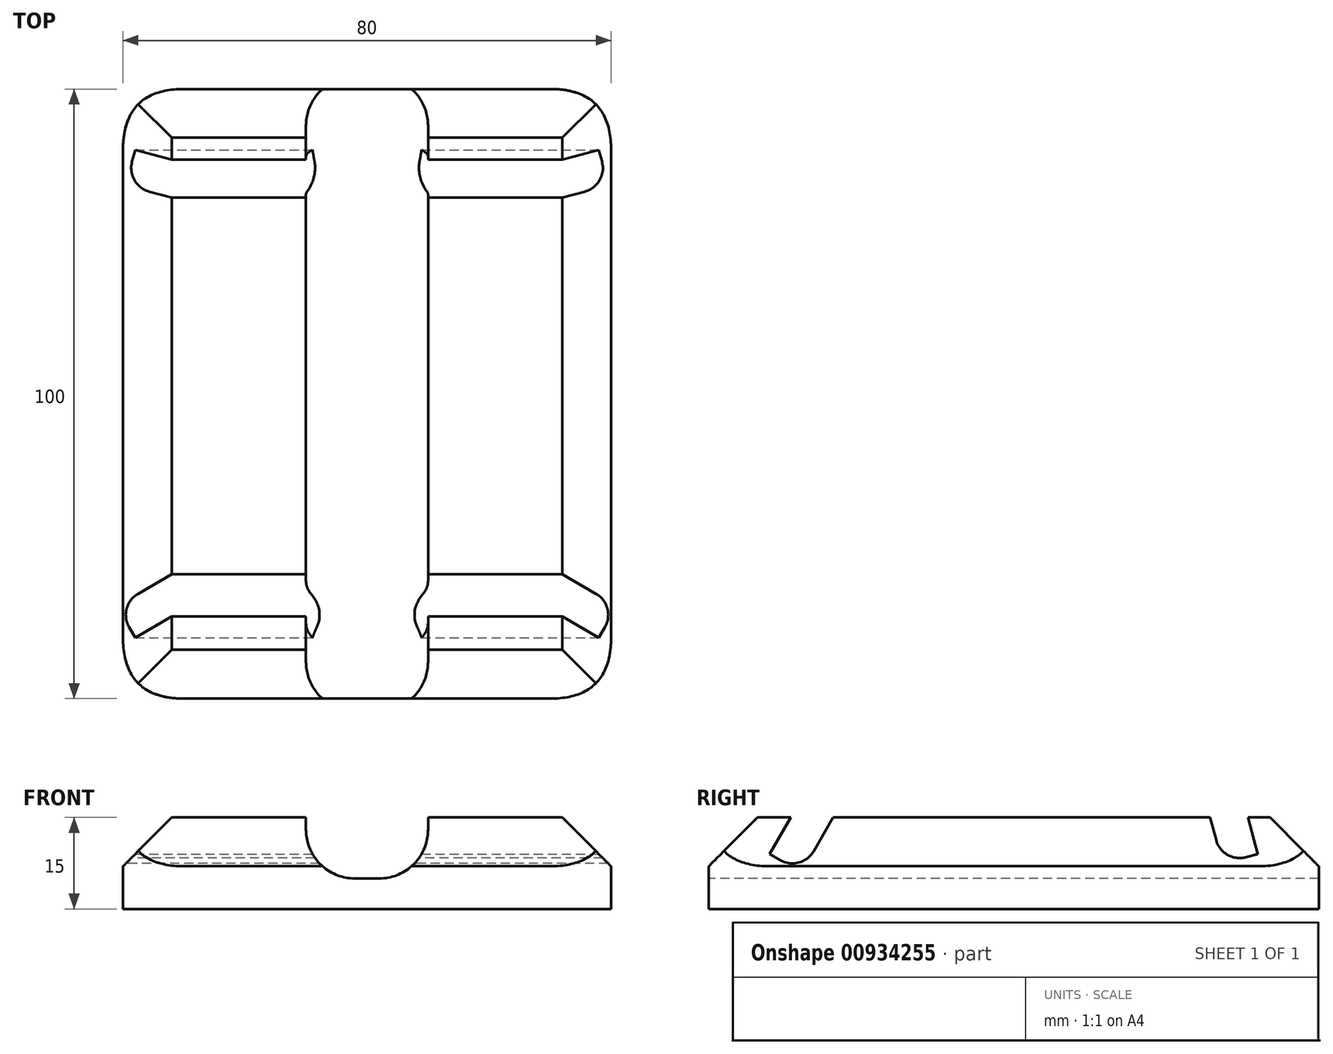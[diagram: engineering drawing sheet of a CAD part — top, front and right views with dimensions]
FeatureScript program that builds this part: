
annotation { "Feature Type Name" : "Feature", "Feature Type Description" : "" }
export const myFeature = defineFeature(function(context is Context, id is Id, definition is map)
    precondition{}
    {
        {
            var Q0;
            Q0=qCreatedBy(makeId("Right.planeOp"),FACE);
            var sketch = newSketch(context, id + "F0", { "sketchPlane" : qUnion([Q0])});
            skLineSegment(sketch, "E0.bottom", {"start": v(100, 15) * mm, "end": v(0, 15) * mm});
            skLineSegment(sketch, "E0.top", {"start": v(100, 0) * mm, "end": v(0, 0) * mm});
            skLineSegment(sketch, "E0.left", {"start": v(100, 15) * mm, "end": v(100, 0) * mm});
            skLineSegment(sketch, "E0.right", {"start": v(0, 15) * mm, "end": v(0, 0) * mm});
            skSolve(sketch);
        }
        {
            var Q0;
            Q0=makeQuery(id+"F0.imprint","IMPRINT",FACE,{"disambiguationData":[TD([[makeQuery(id+"F0.imprint","IMPRINT",EDGE,{"derivedFrom":sQuery(id+"F0.wireOp",EDGE,"E0.bottom")}),1.0]])]});
            var Q1;
            Q1=sQuery(id+"F0.wireOp",EDGE,"E0.bottom");
            var Q2;
            Q2 = qBodyType(qCreatedBy(id + "F0" ,EDGE), BodyType.WIRE);
            extrude(context, id + "F1", {"entities" : qUnion([Q0]), "surfaceEntities" : qUnion([Q1, Q2]), "endBound" : BoundingType.SYMMETRIC, "depth" : 80 * mm, "offsetDistance" : 25 * mm});
        }
        {
            var Q0;
            Q0=qCreatedBy(makeId("Right.planeOp"),FACE);
            var sketch = newSketch(context, id + "F2", { "sketchPlane" : qUnion([Q0])});
            skLineSegment(sketch, "E1", {"start": v(71.28, 9) * mm, "end": v(-12.51, 9) * mm, "construction": true});
            skLineSegment(sketch, "E2", {"start": v(10, 9) * mm, "end": v(97.5, 160.55) * mm, "construction": true});
            skLineSegment(sketch, "E3", {"start": v(90, 9) * mm, "end": v(44.7, 178.04) * mm, "construction": true});
            skLineSegment(sketch, "E4", {"start": v(44.7, 178.04) * mm, "end": v(25.3, 250.48) * mm, "construction": true});
            skLineSegment(sketch, "E5", {"start": v(135, 225.5) * mm, "end": v(97.5, 160.55) * mm, "construction": true});
            skSolve(sketch);
        }
        {
            var Q0;
            Q0=qCreatedBy(makeId("Right.planeOp"),FACE);
            var sketch = newSketch(context, id + "F3", { "sketchPlane" : qUnion([Q0])});
            skLineSegment(sketch, "E6", {"start": v(10, 9) * mm, "end": v(27.02, 38.48) * mm});
            skLineSegment(sketch, "E7", {"start": v(27.02, 38.48) * mm, "end": v(32.22, 35.48) * mm});
            skLineSegment(sketch, "E8", {"start": v(32.22, 35.48) * mm, "end": v(15.2, 6) * mm});
            skLineSegment(sketch, "E9", {"start": v(15.2, 6) * mm, "end": v(10, 9) * mm});
            skLineSegment(sketch, "E10", {"start": v(90, 9) * mm, "end": v(81.3, 41.48) * mm});
            skLineSegment(sketch, "E11", {"start": v(81.3, 41.48) * mm, "end": v(75.5, 39.93) * mm});
            skLineSegment(sketch, "E12", {"start": v(75.5, 39.93) * mm, "end": v(84.2, 7.45) * mm});
            skLineSegment(sketch, "E13", {"start": v(84.2, 7.45) * mm, "end": v(90, 9) * mm});
            skSolve(sketch);
        }
        {
            var Q0;
            Q0=makeQuery(id+"F1.opExtrude","CAP_EDGE",EDGE,{"disambiguationData":[OSD([sQuery(id+"F0.wireOp",EDGE,"E0.bottom")])],"isStart":false});
            var Q1;
            Q1=makeQuery(id+"F1.opExtrude","SWEPT_EDGE",EDGE,{"disambiguationData":[OSD([sQuery(id+"F0.wireOp",EDGE,"E0.bottom"),sQuery(id+"F0.wireOp",EDGE,"E0.right")])]});
            var Q2;
            Q2=makeQuery(id+"F1.opExtrude","CAP_EDGE",EDGE,{"disambiguationData":[OSD([sQuery(id+"F0.wireOp",EDGE,"E0.bottom")])],"isStart":true});
            var Q3;
            Q3=makeQuery(id+"F1.opExtrude","SWEPT_EDGE",EDGE,{"disambiguationData":[OSD([sQuery(id+"F0.wireOp",EDGE,"E0.bottom"),sQuery(id+"F0.wireOp",EDGE,"E0.left")])]});
            chamfer(context, id + "F4", {"entities" : qUnion([Q0, Q1, Q2, Q3]), "width" : 8 * mm, "tangentPropagation" : true});
        }
        {
            var Q0;
            Q0 = qSketchRegion(id + "F3", true);
            extrude(context, id + "F5", {"entities" : qUnion([Q0]), "operationType" : NewBodyOperationType.REMOVE, "endBound" : BoundingType.THROUGH_ALL, "oppositeDirection" : true, "depth" : 25 * mm, "offsetDistance" : 25 * mm, "hasSecondDirection" : true, "secondDirectionBound" : SecondDirectionBoundingType.THROUGH_ALL, "secondDirectionOppositeDirection" : false, "secondDirectionDepth" : 25 * mm});
        }
        {
            var Q0;
            Q0=makeQuery(id+"F1.opExtrude","SWEPT_FACE",FACE,{"disambiguationData":[OSD([sQuery(id+"F0.wireOp",EDGE,"E0.right")])]});
            var sketch = newSketch(context, id + "F6", { "sketchPlane" : qUnion([Q0])});
            skLineSegment(sketch, "E14.bottom", {"start": v(-10, 15) * mm, "end": v(10, 15) * mm});
            skLineSegment(sketch, "E14.top", {"start": v(-10, 5) * mm, "end": v(10, 5) * mm});
            skLineSegment(sketch, "E14.left", {"start": v(-10, 15) * mm, "end": v(-10, 5) * mm});
            skLineSegment(sketch, "E14.right", {"start": v(10, 15) * mm, "end": v(10, 5) * mm});
            skSolve(sketch);
        }
        {
            var Q0;
            Q0 = qSketchRegion(id + "F6", true);
            extrude(context, id + "F7", {"entities" : qUnion([Q0]), "operationType" : NewBodyOperationType.REMOVE, "endBound" : BoundingType.THROUGH_ALL, "oppositeDirection" : true, "depth" : 25 * mm, "offsetDistance" : 25 * mm});
        }
        {
            var Q0;
            Q0=makeQuery(id+"F1.opExtrude","CAP_EDGE",EDGE,{"disambiguationData":[OSD([sQuery(id+"F0.wireOp",EDGE,"E0.right")])],"isStart":false});
            var Q1;
            Q1=makeQuery(id+"F1.opExtrude","CAP_EDGE",EDGE,{"disambiguationData":[OSD([sQuery(id+"F0.wireOp",EDGE,"E0.right")])],"isStart":true});
            var Q2;
            Q2=makeQuery(id+"F1.opExtrude","CAP_EDGE",EDGE,{"disambiguationData":[OSD([sQuery(id+"F0.wireOp",EDGE,"E0.left")])],"isStart":true});
            var Q3;
            Q3=makeQuery(id+"F1.opExtrude","CAP_EDGE",EDGE,{"disambiguationData":[OSD([sQuery(id+"F0.wireOp",EDGE,"E0.left")])],"isStart":false});
            fillet(context, id + "F8", {"entities" : qUnion([Q0, Q1, Q2, Q3]), "radius" : 10 * mm, "tangentPropagation" : true, "rho" : 0.5, "crossSection" : FilletCrossSection.CONIC, "allowEdgeOverflow" : false});
        }
        {
            var Q0;
            {var subQ0=sQuery(id+"F3.wireOp",EDGE,"E8");var subQ1=sQuery(id+"F3.wireOp",EDGE,"E9");Q0=makeQuery(id+"F7.boolean.opBoolean","SPLIT",EDGE,{"disambiguationData":[TD([makeQuery(id+"F7.opExtrude","SWEPT_FACE",FACE,{"disambiguationData":[OSD([sQuery(id+"F6.wireOp",EDGE,"E14.left")])]})])],"derivedFrom":makeQuery(id+"F5.boolean.opBoolean","COPY",EDGE,{"derivedFrom":makeQuery(id+"F5.opExtrude","SWEPT_EDGE",EDGE,{"disambiguationData":[OSD([subQ0,subQ1])]})})});}
            var Q1;
            {var subQ0=sQuery(id+"F3.wireOp",EDGE,"E9");var subQ1=sQuery(id+"F3.wireOp",EDGE,"E8");Q1=makeQuery(id+"F7.boolean.opBoolean","SPLIT",EDGE,{"disambiguationData":[TD([makeQuery(id+"F7.opExtrude","SWEPT_FACE",FACE,{"disambiguationData":[OSD([sQuery(id+"F6.wireOp",EDGE,"E14.right")])]})])],"derivedFrom":makeQuery(id+"F5.boolean.opBoolean","COPY",EDGE,{"derivedFrom":makeQuery(id+"F5.opExtrude","SWEPT_EDGE",EDGE,{"disambiguationData":[OSD([subQ1,subQ0])]})})});}
            var Q2;
            {var subQ0=sQuery(id+"F3.wireOp",EDGE,"E12");var subQ1=sQuery(id+"F3.wireOp",EDGE,"E13");Q2=makeQuery(id+"F7.boolean.opBoolean","SPLIT",EDGE,{"disambiguationData":[TD([makeQuery(id+"F7.opExtrude","SWEPT_FACE",FACE,{"disambiguationData":[OSD([sQuery(id+"F6.wireOp",EDGE,"E14.left")])]})])],"derivedFrom":makeQuery(id+"F5.boolean.opBoolean","COPY",EDGE,{"derivedFrom":makeQuery(id+"F5.opExtrude","SWEPT_EDGE",EDGE,{"disambiguationData":[OSD([subQ0,subQ1])]})})});}
            var Q3;
            {var subQ0=sQuery(id+"F3.wireOp",EDGE,"E12");var subQ1=sQuery(id+"F3.wireOp",EDGE,"E13");Q3=makeQuery(id+"F7.boolean.opBoolean","SPLIT",EDGE,{"disambiguationData":[TD([makeQuery(id+"F7.opExtrude","SWEPT_FACE",FACE,{"disambiguationData":[OSD([sQuery(id+"F6.wireOp",EDGE,"E14.right")])]})])],"derivedFrom":makeQuery(id+"F5.boolean.opBoolean","COPY",EDGE,{"derivedFrom":makeQuery(id+"F5.opExtrude","SWEPT_EDGE",EDGE,{"disambiguationData":[OSD([subQ0,subQ1])]})})});}
            fillet(context, id + "F9", {"entities" : qUnion([Q0, Q1, Q2, Q3]), "radius" : 4 * mm, "tangentPropagation" : true, "allowEdgeOverflow" : false});
        }
        {
            var Q0;
            Q0=makeQuery(id+"F7.boolean.opBoolean","COPY",EDGE,{"derivedFrom":makeQuery(id+"F7.opExtrude","SWEPT_EDGE",EDGE,{"disambiguationData":[OSD([sQuery(id+"F6.wireOp",EDGE,"E14.top"),sQuery(id+"F6.wireOp",EDGE,"E14.left")])]})});
            var Q1;
            Q1=makeQuery(id+"F7.boolean.opBoolean","COPY",EDGE,{"derivedFrom":makeQuery(id+"F7.opExtrude","SWEPT_EDGE",EDGE,{"disambiguationData":[OSD([sQuery(id+"F6.wireOp",EDGE,"E14.top"),sQuery(id+"F6.wireOp",EDGE,"E14.right")])]})});
            fillet(context, id + "F10", {"entities" : qUnion([Q0, Q1]), "radius" : 8 * mm, "tangentPropagation" : true, "allowEdgeOverflow" : false});
        }
    });
